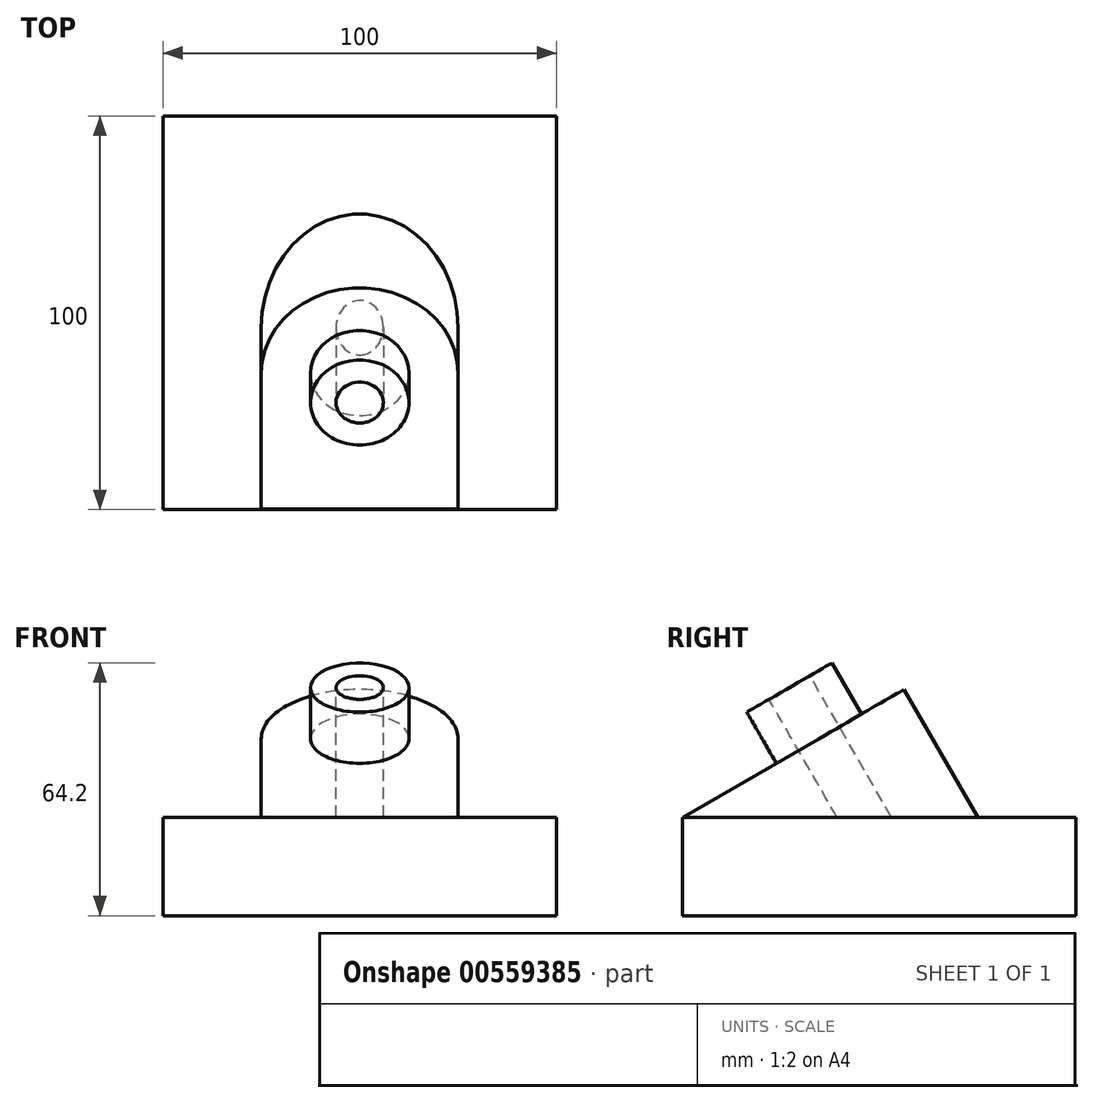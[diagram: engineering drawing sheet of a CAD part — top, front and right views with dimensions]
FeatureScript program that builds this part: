
annotation { "Feature Type Name" : "Feature", "Feature Type Description" : "" }
export const myFeature = defineFeature(function(context is Context, id is Id, definition is map)
    precondition{}
    {
        {
            var Q0;
            Q0=qCreatedBy(makeId("Front.planeOp"),FACE);
            var sketch = newSketch(context, id + "F0", { "sketchPlane" : qUnion([Q0])});
            skLineSegment(sketch, "E0.bottom", {"start": v(0, 0) * mm, "end": v(100, 0) * mm});
            skLineSegment(sketch, "E0.top", {"start": v(0, -25) * mm, "end": v(100, -25) * mm});
            skLineSegment(sketch, "E0.left", {"start": v(0, 0) * mm, "end": v(0, -25) * mm});
            skLineSegment(sketch, "E0.right", {"start": v(100, 0) * mm, "end": v(100, -25) * mm});
            skSolve(sketch);
        }
        {
            var Q0;
            Q0 = qSketchRegion(id + "F0", true);
            extrude(context, id + "F1", {"entities" : qUnion([Q0]), "depth" : 100 * mm, "offsetDistance" : 25 * mm});
        }
        {
            var Q0;
            Q0=makeQuery(id+"F1.opExtrude","SWEPT_FACE",FACE,{"disambiguationData":[OSD([sQuery(id+"F0.wireOp",EDGE,"E0.bottom")])]});
            var sketch = newSketch(context, id + "F2", { "sketchPlane" : qUnion([Q0])});
            skLineSegment(sketch, "E1.bottom", {"start": v(25, -100) * mm, "end": v(75, -100) * mm});
            skLineSegment(sketch, "E1.top", {"start": v(25, -60) * mm, "end": v(75, -60) * mm});
            skLineSegment(sketch, "E1.left", {"start": v(25, -100) * mm, "end": v(25, -60) * mm});
            skLineSegment(sketch, "E1.right", {"start": v(75, -100) * mm, "end": v(75, -60) * mm});
            skSolve(sketch);
        }
        {
            var Q0;
            Q0=makeQuery(id+"F2.imprint","IMPRINT",FACE,{"disambiguationData":[TD([[makeQuery(id+"F2.imprint","IMPRINT",EDGE,{"derivedFrom":sQuery(id+"F2.wireOp",EDGE,"E1.top")}),1.0]])]});
            var sketch = newSketch(context, id + "F3", { "sketchPlane" : qUnion([Q0])});
            skCircle(sketch, "E2", {"center": v(50, -60) * mm, "radius": 25 * mm});
            skSolve(sketch);
        }
        {
            var Q0;
            Q0=makeQuery(id+"F2.imprint","IMPRINT",FACE,{"disambiguationData":[TD([[makeQuery(id+"F2.imprint","IMPRINT",EDGE,{"derivedFrom":sQuery(id+"F2.wireOp",EDGE,"E1.bottom")}),1.0]])]});
            var sketch = newSketch(context, id + "F4", { "sketchPlane" : qUnion([Q0])});
            skCircle(sketch, "E3", {"center": v(50, -60) * mm, "radius": 12.5 * mm});
            skSolve(sketch);
        }
        {
            var Q0;
            Q0=qCreatedBy(makeId("Right.planeOp"),FACE);
            var sketch = newSketch(context, id + "F5", { "sketchPlane" : qUnion([Q0])});
            skLineSegment(sketch, "E4", {"start": v(-99.9, 0) * mm, "end": v(-33.36, 38.42) * mm});
            skSolve(sketch);
        }
        {
            var Q0;
            Q0=sQuery(id+"F5.wireOp",EDGE,"E4");
            cPlane(context, id + "F6", {"entities" : qUnion([Q0]), "cplaneType" : CPlaneType.LINE_ANGLE, "offset" : 25 * mm, "angle" : 0 * degree, "width" : 150 * mm, "height" : 150 * mm});
        }
        {
            var Q0;
            Q0=qCreatedBy(id+"F6.planeOp",FACE);
            var sketch = newSketch(context, id + "F7", { "sketchPlane" : qUnion([Q0])});
            skLineSegment(sketch, "E5.bottom", {"start": v(25, -86.6) * mm, "end": v(75, -86.6) * mm});
            skLineSegment(sketch, "E5.top", {"start": v(25, -46.6) * mm, "end": v(75, -46.6) * mm});
            skLineSegment(sketch, "E5.left", {"start": v(25, -86.6) * mm, "end": v(25, -46.6) * mm});
            skLineSegment(sketch, "E5.right", {"start": v(75, -86.6) * mm, "end": v(75, -46.6) * mm});
            skSolve(sketch);
        }
        {
            var Q0;
            Q0=qCreatedBy(id+"F6.planeOp",FACE);
            var sketch = newSketch(context, id + "F8", { "sketchPlane" : qUnion([Q0])});
            skCircle(sketch, "E6", {"center": v(50, -46.6) * mm, "radius": 25 * mm});
            skSolve(sketch);
        }
        {
            var Q0;
            Q0=qCreatedBy(id+"F6.planeOp",FACE);
            var sketch = newSketch(context, id + "F9", { "sketchPlane" : qUnion([Q0])});
            skCircle(sketch, "E7", {"center": v(50, -46.6) * mm, "radius": 12.5 * mm});
            skSolve(sketch);
        }
        {
            var Q0;
            Q0=qCreatedBy(id+"F6.planeOp",FACE);
            var sketch = newSketch(context, id + "F10", { "sketchPlane" : qUnion([Q0])});
            skCircle(sketch, "E8", {"center": v(50, -46.6) * mm, "radius": 6 * mm});
            skSolve(sketch);
        }
        {
            var Q0;
            Q0=makeQuery(id+"F7.imprint","IMPRINT",FACE,{"disambiguationData":[TD([[makeQuery(id+"F7.imprint","IMPRINT",EDGE,{"derivedFrom":sQuery(id+"F7.wireOp",EDGE,"E5.bottom")}),1.0]])]});
            var Q1;
            Q1=makeQuery(id+"F8.imprint","IMPRINT",FACE,{"disambiguationData":[TD([[makeQuery(id+"F8.imprint","IMPRINT",EDGE,{"derivedFrom":sQuery(id+"F8.wireOp",EDGE,"E6")}),1.0]])]});
            extrude(context, id + "F11", {"entities" : qUnion([Q0, Q1]), "operationType" : NewBodyOperationType.ADD, "endBound" : BoundingType.UP_TO_NEXT, "oppositeDirection" : true, "depth" : 35 * mm, "offsetDistance" : 25 * mm});
        }
        {
            var Q0;
            Q0=makeQuery(id+"F9.imprint","IMPRINT",FACE,{"disambiguationData":[TD([[makeQuery(id+"F9.imprint","IMPRINT",EDGE,{"derivedFrom":sQuery(id+"F9.wireOp",EDGE,"E7")}),1.0]])]});
            extrude(context, id + "F12", {"entities" : qUnion([Q0]), "operationType" : NewBodyOperationType.ADD, "depth" : 15 * mm, "offsetDistance" : 25 * mm});
        }
        {
            var Q0;
            Q0=makeQuery(id+"F12.opExtrude","CAP_FACE",FACE,{"disambiguationData":[OSD([sQuery(id+"F9.wireOp",EDGE,"E7")])],"isStart":false});
            var sketch = newSketch(context, id + "F13", { "sketchPlane" : qUnion([Q0])});
            skCircle(sketch, "E9", {"center": v(50, -46.6) * mm, "radius": 6 * mm});
            skSolve(sketch);
        }
        {
            var Q0;
            Q0=makeQuery(id+"F13.imprint","IMPRINT",FACE,{"disambiguationData":[TD([[makeQuery(id+"F13.imprint","IMPRINT",EDGE,{"derivedFrom":sQuery(id+"F13.wireOp",EDGE,"E9")}),1.0]])]});
            var Q1;
            Q1=sQuery(id+"F13.wireOp",EDGE,"E9");
            var Q2;
            Q2=qCreatedBy(makeId("Top.planeOp"),FACE);
            extrude(context, id + "F14", {"entities" : qUnion([Q0]), "operationType" : NewBodyOperationType.REMOVE, "surfaceEntities" : qUnion([Q1]), "endBound" : BoundingType.UP_TO_SURFACE, "oppositeDirection" : true, "depth" : 25 * mm, "endBoundEntityFace" : qUnion([Q2]), "offsetDistance" : 25 * mm});
        }
    });
